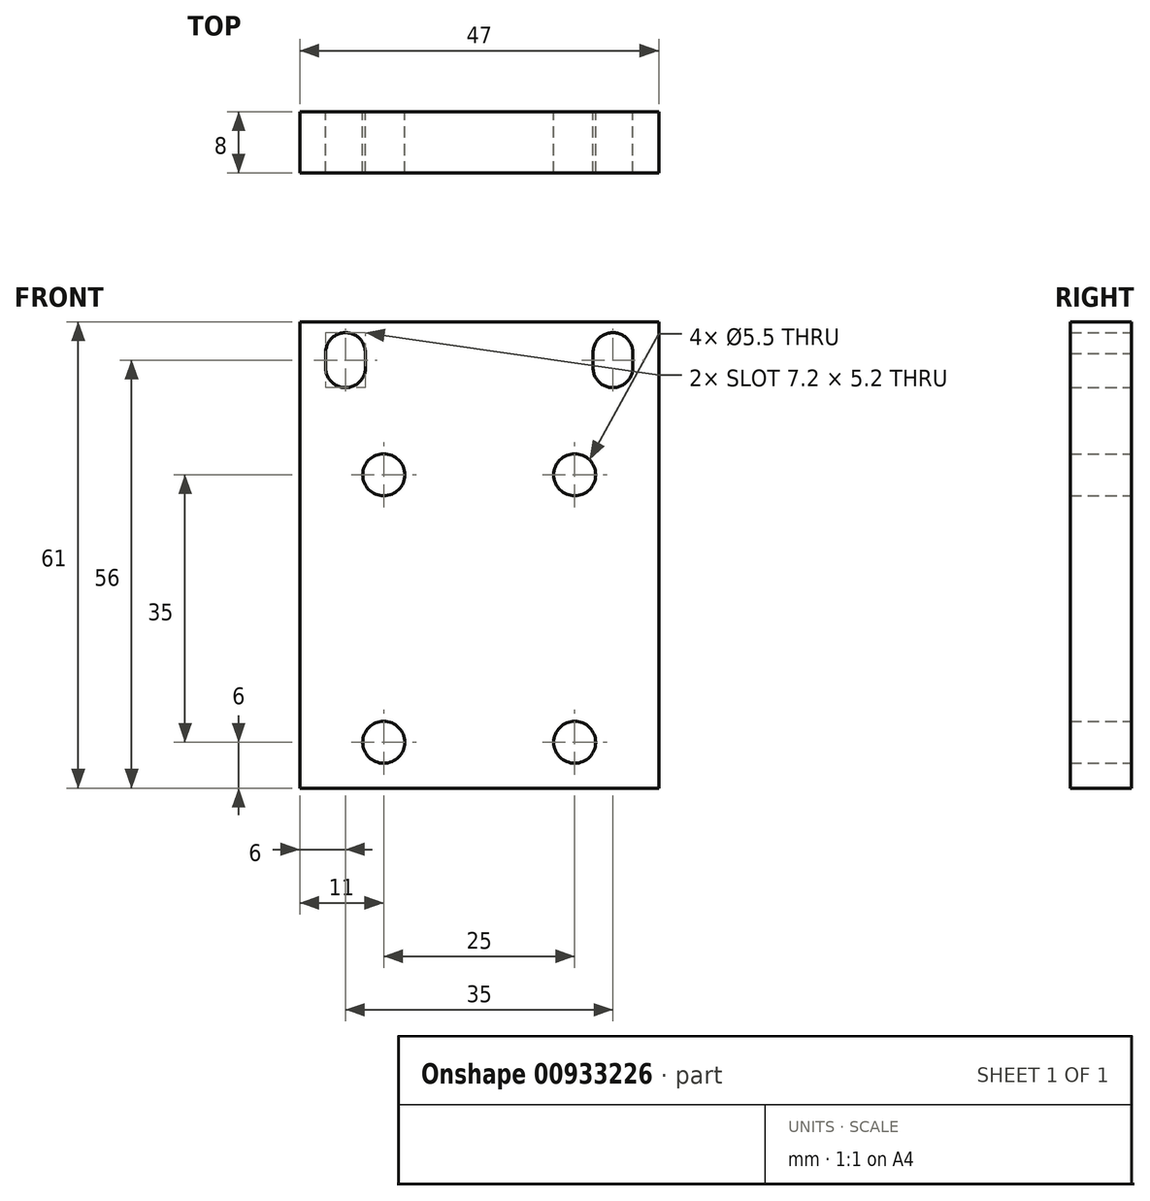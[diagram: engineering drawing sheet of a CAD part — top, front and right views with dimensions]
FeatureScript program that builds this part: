
annotation { "Feature Type Name" : "Feature", "Feature Type Description" : "" }
export const myFeature = defineFeature(function(context is Context, id is Id, definition is map)
    precondition{}
    {
        {
            var Q0;
            Q0=qCreatedBy(makeId("Front.planeOp"),FACE);
            var sketch = newSketch(context, id + "F0", { "sketchPlane" : qUnion([Q0])});
            skLineSegment(sketch, "E0.bottom", {"start": v(-23.5, 30.5) * mm, "end": v(23.5, 30.5) * mm});
            skLineSegment(sketch, "E0.top", {"start": v(-23.5, -30.5) * mm, "end": v(23.5, -30.5) * mm});
            skLineSegment(sketch, "E0.left", {"start": v(-23.5, 30.5) * mm, "end": v(-23.5, -30.5) * mm});
            skLineSegment(sketch, "E0.right", {"start": v(23.5, 30.5) * mm, "end": v(23.5, -30.5) * mm});
            skPoint(sketch, "E0.middle", {"position": v(0, 0) * mm});
            skCircle(sketch, "E1", {"center": v(12.5, -24.5) * mm, "radius": 2.75 * mm});
            skCircle(sketch, "E2", {"center": v(12.5, 10.5) * mm, "radius": 2.75 * mm});
            skCircle(sketch, "E3.MirrorC", {"center": v(-12.5, 10.5) * mm, "radius": 2.75 * mm});
            skCircle(sketch, "E4.MirrorC", {"center": v(-12.5, -24.5) * mm, "radius": 2.75 * mm});
            skLineSegment(sketch, "E5", {"start": v(-23.5, 16.5) * mm, "end": v(23.5, 16.5) * mm, "construction": true});
            skLineSegment(sketch, "E6", {"start": v(-23.5, 20.5) * mm, "end": v(-10, 20.5) * mm, "construction": true});
            skArc(sketch, "E7", {"start": v(-20.1, 24.51) * mm, "mid": v(-17.5, 21.9) * mm, "end": v(-14.9, 24.5) * mm});
            skLineSegment(sketch, "E8", {"start": v(-14.9, 26.37) * mm, "end": v(-14.9, 24.5) * mm});
            skLineSegment(sketch, "E9", {"start": v(-20.1, 24.51) * mm, "end": v(-20.1, 26.5) * mm});
            skArc(sketch, "E10.trimOffspring", {"start": v(-14.9, 26.37) * mm, "mid": v(-17.43, 29.1) * mm, "end": v(-20.1, 26.5) * mm});
            skArc(sketch, "E11.MirrorCS", {"start": v(20.1, 24.51) * mm, "mid": v(17.5, 21.9) * mm, "end": v(14.9, 24.5) * mm});
            skArc(sketch, "E12.MirrorCS", {"start": v(14.9, 26.37) * mm, "mid": v(17.43, 29.1) * mm, "end": v(20.1, 26.5) * mm});
            skLineSegment(sketch, "E13.MirrorCS", {"start": v(20.1, 24.51) * mm, "end": v(20.1, 26.5) * mm});
            skLineSegment(sketch, "E14.MirrorCS", {"start": v(14.9, 26.37) * mm, "end": v(14.9, 24.5) * mm});
            skLineSegment(sketch, "E15.bottom", {"start": v(5.88, 25.5) * mm, "end": v(-5.88, 25.5) * mm, "construction": true});
            skLineSegment(sketch, "E15.top", {"start": v(5.88, 20.5) * mm, "end": v(-5.88, 20.5) * mm, "construction": true});
            skLineSegment(sketch, "E15.left", {"start": v(10, 24.47) * mm, "end": v(10, 21.53) * mm, "construction": true});
            skLineSegment(sketch, "E15.right", {"start": v(-10, 24.47) * mm, "end": v(-10, 21.53) * mm, "construction": true});
            skPoint(sketch, "E15.middle", {"position": v(0, 23) * mm});
            skArc(sketch, "E16", {"start": v(-9.76, 26.47) * mm, "mid": v(-10.97, 25.74) * mm, "end": v(-10.24, 24.53) * mm, "construction": true});
            skArc(sketch, "E17", {"start": v(-10.24, 21.47) * mm, "mid": v(-10.97, 20.26) * mm, "end": v(-9.76, 19.53) * mm, "construction": true});
            skArc(sketch, "E18", {"start": v(10.24, 24.53) * mm, "mid": v(10.97, 25.74) * mm, "end": v(9.76, 26.47) * mm, "construction": true});
            skArc(sketch, "E19", {"start": v(9.76, 19.53) * mm, "mid": v(10.97, 20.26) * mm, "end": v(10.24, 21.47) * mm, "construction": true});
            skLineSegment(sketch, "E20.trimOffspring", {"start": v(10, 20.5) * mm, "end": v(23.5, 20.5) * mm, "construction": true});
            skLineSegment(sketch, "E21.trimOffspring", {"start": v(-5.88, 20.5) * mm, "end": v(5.88, 20.5) * mm, "construction": true});
            skLineSegment(sketch, "E22", {"start": v(-9.76, 26.47) * mm, "end": v(-5.88, 25.5) * mm, "construction": true});
            skLineSegment(sketch, "E23", {"start": v(-10.24, 24.53) * mm, "end": v(-10, 24.47) * mm, "construction": true});
            skLineSegment(sketch, "E24", {"start": v(-10.24, 21.47) * mm, "end": v(-10, 21.53) * mm, "construction": true});
            skLineSegment(sketch, "E25", {"start": v(-9.76, 19.53) * mm, "end": v(-5.88, 20.5) * mm, "construction": true});
            skLineSegment(sketch, "E26.trimOffspring", {"start": v(10, 24.47) * mm, "end": v(10.24, 24.53) * mm, "construction": true});
            skLineSegment(sketch, "E27.trimOffspring", {"start": v(5.88, 25.5) * mm, "end": v(9.76, 26.47) * mm, "construction": true});
            skLineSegment(sketch, "E28.trimOffspring", {"start": v(5.88, 20.5) * mm, "end": v(9.76, 19.53) * mm, "construction": true});
            skLineSegment(sketch, "E29.trimOffspring", {"start": v(10, 21.53) * mm, "end": v(10.24, 21.47) * mm, "construction": true});
            skSolve(sketch);
        }
        {
            var Q0;
            Q0 = qSketchRegion(id + "F0", true);
            extrude(context, id + "F1", {"entities" : qUnion([Q0]), "depth" : 8 * mm, "offsetDistance" : 25 * mm});
        }
    });
